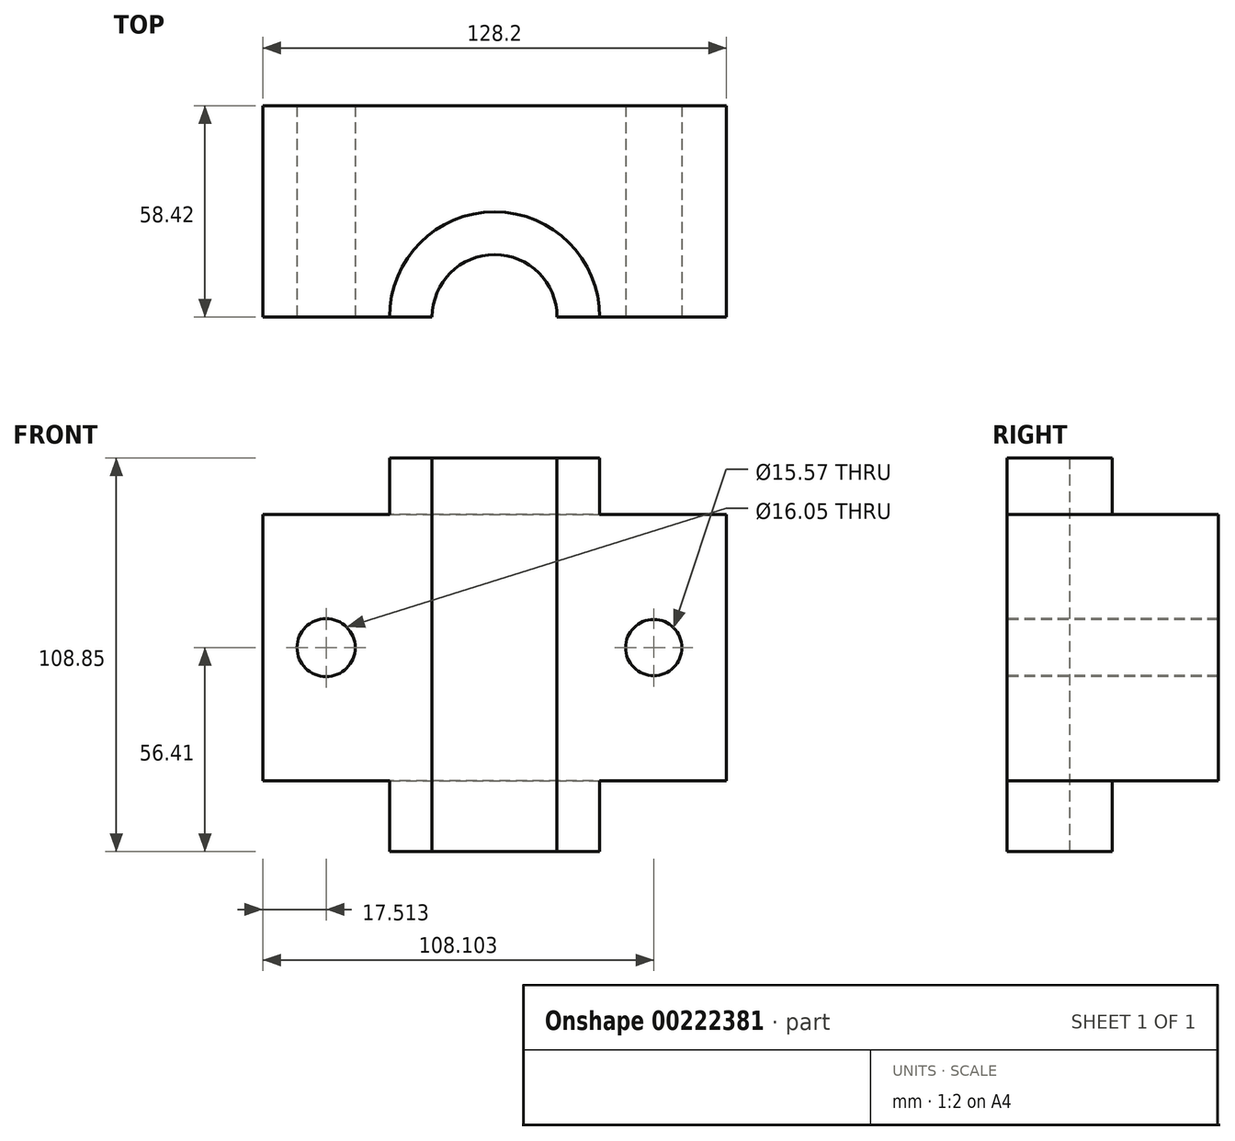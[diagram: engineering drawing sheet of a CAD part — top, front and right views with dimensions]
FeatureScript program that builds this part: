
annotation { "Feature Type Name" : "Feature", "Feature Type Description" : "" }
export const myFeature = defineFeature(function(context is Context, id is Id, definition is map)
    precondition{}
    {
        {
            var Q0;
            Q0=qCreatedBy(makeId("Front.planeOp"),FACE);
            var sketch = newSketch(context, id + "F0", { "sketchPlane" : qUnion([Q0])});
            skLineSegment(sketch, "E0.bottom", {"start": v(64.1, -36.89) * mm, "end": v(-64.1, -36.89) * mm});
            skLineSegment(sketch, "E0.top", {"start": v(64.1, 36.89) * mm, "end": v(-64.1, 36.89) * mm});
            skLineSegment(sketch, "E0.left", {"start": v(64.1, -36.89) * mm, "end": v(64.1, 36.89) * mm});
            skLineSegment(sketch, "E0.right", {"start": v(-64.1, -36.89) * mm, "end": v(-64.1, 36.89) * mm});
            skPoint(sketch, "E0.middle", {"position": v(0, 0) * mm});
            skSolve(sketch);
        }
        {
            var Q0;
            Q0=makeQuery(id+"F0.imprint","IMPRINT",FACE,{"disambiguationData":[TD([[makeQuery(id+"F0.imprint","IMPRINT",EDGE,{"derivedFrom":sQuery(id+"F0.wireOp",EDGE,"E0.bottom")}),-1.0]])]});
            extrude(context, id + "F1", {"entities" : qUnion([Q0]), "depth" : 58.42 * mm});
        }
        {
            var Q0;
            Q0=makeQuery(id+"F1.opExtrude","SWEPT_FACE",FACE,{"disambiguationData":[OSD([sQuery(id+"F0.wireOp",EDGE,"E0.bottom")])]});
            var sketch = newSketch(context, id + "F6", { "sketchPlane" : qUnion([Q0])});
            skCircle(sketch, "E1", {"center": v(0, 58.42) * mm, "radius": 29.07 * mm});
            skSolve(sketch);
        }
        {
            var Q0;
            {var subQ0=sQuery(id+"F6.wireOp",EDGE,"E1");var subQ1=makeQuery(id+"F1.opExtrude","CAP_EDGE",EDGE,{"disambiguationData":[OSD([sQuery(id+"F0.wireOp",EDGE,"E0.bottom")])],"isStart":false});var subQ2=makeQuery(id+"F6.imprint","INTERSECT",VERTEX,{"disambiguationData":[OD(0.0)],"derivedFrom":[subQ1,subQ0]});Q0=makeQuery(id+"F6.imprint","IMPRINT",FACE,{"disambiguationData":[TD([[makeQuery(id+"F6.imprint","IMPRINT",EDGE,{"disambiguationData":[TD([[subQ2,1.0]])],"derivedFrom":subQ0}),1.0]])]});}
            extrude(context, id + "F2", {"entities" : qUnion([Q0]), "operationType" : NewBodyOperationType.ADD, "depth" : 19.52 * mm, "hasSecondDirection" : true, "secondDirectionOppositeDirection" : true, "secondDirectionDepth" : 89.32 * mm});
        }
        {
            var Q0;
            Q0=makeQuery(id+"F1.opExtrude","SWEPT_FACE",FACE,{"disambiguationData":[OSD([sQuery(id+"F0.wireOp",EDGE,"E0.bottom")])]});
            var sketch = newSketch(context, id + "F7", { "sketchPlane" : qUnion([Q0])});
            skCircle(sketch, "E2", {"center": v(0, 58.42) * mm, "radius": 17.27 * mm});
            skSolve(sketch);
        }
        {
            var Q0;
            Q0=makeQuery(id+"F7.imprint","IMPRINT",FACE,{"disambiguationData":[TD([[makeQuery(id+"F7.imprint","IMPRINT",EDGE,{"derivedFrom":sQuery(id+"F7.wireOp",EDGE,"E2")}),1.0]])]});
            extrude(context, id + "F3", {"entities" : qUnion([Q0]), "operationType" : NewBodyOperationType.REMOVE, "endBound" : BoundingType.THROUGH_ALL, "oppositeDirection" : true, "depth" : 25.4 * mm, "hasSecondDirection" : true, "secondDirectionOppositeDirection" : false, "secondDirectionDepth" : 25.4 * mm});
        }
        {
            var Q0;
            {var subQ0=sQuery(id+"F0.wireOp",EDGE,"E0.left");var subQ2=sQuery(id+"F0.wireOp",EDGE,"E0.bottom");var subQ3=sQuery(id+"F0.wireOp",EDGE,"E0.top");Q0=makeQuery(id+"F3.boolean.opBoolean","SPLIT",FACE,{"disambiguationData":[TD([makeQuery(id+"F1.opExtrude","SWEPT_FACE",FACE,{"disambiguationData":[OSD([subQ0])]})])],"derivedFrom":makeQuery(id+"F2.boolean.opBoolean","MERGE",FACE,{"derivedFrom":[makeQuery(id+"F1.opExtrude","CAP_FACE",FACE,{"disambiguationData":[OSD([subQ2,subQ3,subQ0,sQuery(id+"F0.wireOp",EDGE,"E0.right")])],"isStart":false}),makeQuery(id+"F2.opExtrude","SWEPT_FACE",FACE,{"disambiguationData":[OSD([subQ2])]})]})});}
            var sketch = newSketch(context, id + "F8", { "sketchPlane" : qUnion([Q0])});
            skCircle(sketch, "E3", {"center": v(44, 0) * mm, "radius": 7.78 * mm});
            skSolve(sketch);
        }
        {
            var Q0;
            Q0=makeQuery(id+"F8.imprint","IMPRINT",FACE,{"disambiguationData":[TD([[makeQuery(id+"F8.imprint","IMPRINT",EDGE,{"derivedFrom":sQuery(id+"F8.wireOp",EDGE,"E3")}),1.0]])]});
            extrude(context, id + "F4", {"entities" : qUnion([Q0]), "operationType" : NewBodyOperationType.REMOVE, "endBound" : BoundingType.THROUGH_ALL, "oppositeDirection" : true, "depth" : 25.4 * mm});
        }
        {
            var Q0;
            {var subQ0=sQuery(id+"F0.wireOp",EDGE,"E0.right");var subQ2=sQuery(id+"F0.wireOp",EDGE,"E0.top");var subQ3=sQuery(id+"F0.wireOp",EDGE,"E0.bottom");Q0=makeQuery(id+"F3.boolean.opBoolean","SPLIT",FACE,{"disambiguationData":[TD([makeQuery(id+"F1.opExtrude","SWEPT_FACE",FACE,{"disambiguationData":[OSD([subQ0])]})])],"derivedFrom":makeQuery(id+"F2.boolean.opBoolean","MERGE",FACE,{"derivedFrom":[makeQuery(id+"F1.opExtrude","CAP_FACE",FACE,{"disambiguationData":[OSD([subQ3,subQ2,sQuery(id+"F0.wireOp",EDGE,"E0.left"),subQ0])],"isStart":false}),makeQuery(id+"F2.opExtrude","SWEPT_FACE",FACE,{"disambiguationData":[OSD([subQ3])]})]})});}
            var sketch = newSketch(context, id + "F9", { "sketchPlane" : qUnion([Q0])});
            skCircle(sketch, "E4", {"center": v(-46.59, 0) * mm, "radius": 8.03 * mm});
            skPoint(sketch, "E4.centerSnap0", {"position": v(-46.59, 36.89) * mm});
            skSolve(sketch);
        }
        {
            var Q0;
            Q0=makeQuery(id+"F9.imprint","IMPRINT",FACE,{"disambiguationData":[TD([[makeQuery(id+"F9.imprint","IMPRINT",EDGE,{"derivedFrom":sQuery(id+"F9.wireOp",EDGE,"E4")}),1.0]])]});
            extrude(context, id + "F10", {"entities" : qUnion([Q0]), "operationType" : NewBodyOperationType.REMOVE, "endBound" : BoundingType.THROUGH_ALL, "oppositeDirection" : true, "depth" : 25.4 * mm});
        }
    });
